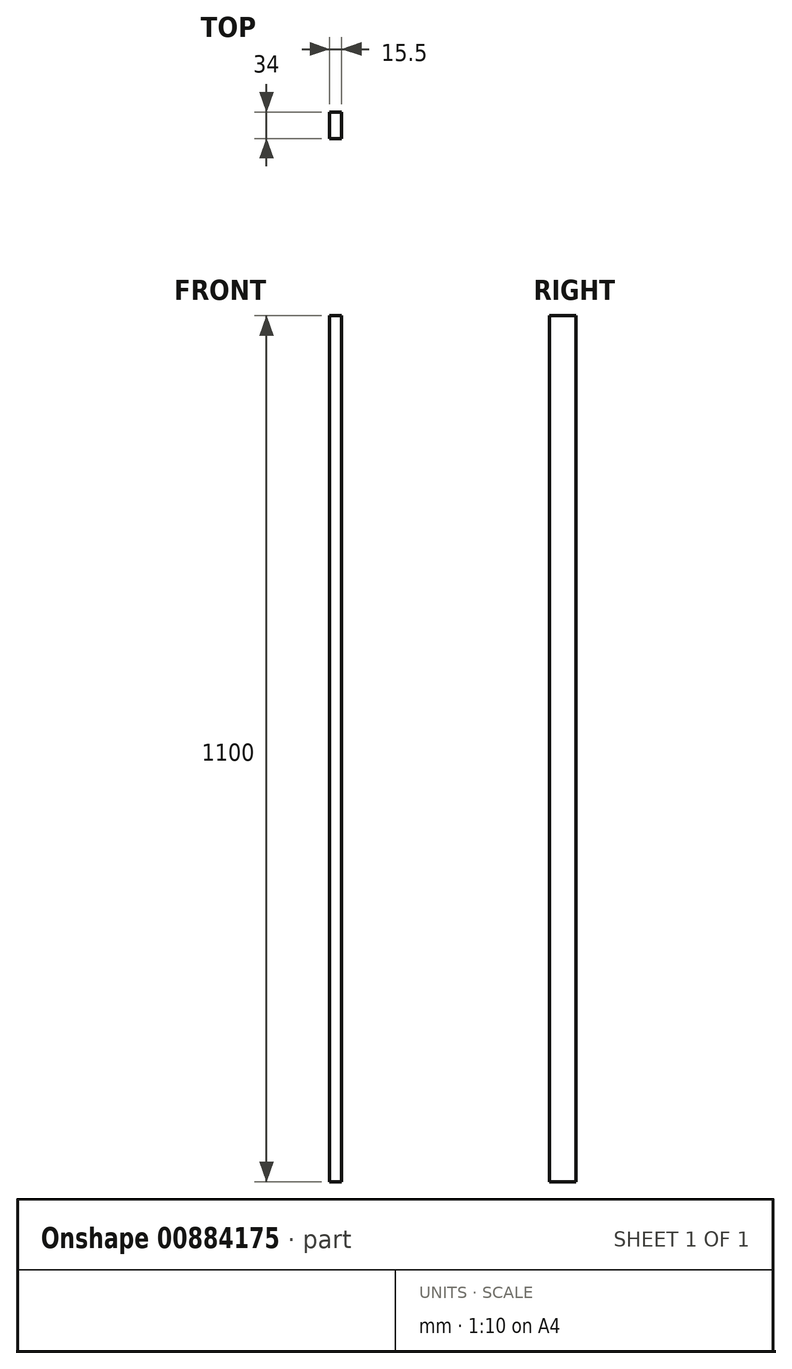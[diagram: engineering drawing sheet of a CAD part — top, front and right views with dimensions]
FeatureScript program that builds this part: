
annotation { "Feature Type Name" : "Feature", "Feature Type Description" : "" }
export const myFeature = defineFeature(function(context is Context, id is Id, definition is map)
    precondition{}
    {
        {
            var Q0;
            Q0=qCreatedBy(makeId("Top.planeOp"),FACE);
            var sketch = newSketch(context, id + "F0", { "sketchPlane" : qUnion([Q0])});
            skLineSegment(sketch, "E0.bottom", {"start": v(0, 0) * mm, "end": v(15.5, 0) * mm});
            skLineSegment(sketch, "E0.top", {"start": v(0, -34) * mm, "end": v(15.5, -34) * mm});
            skLineSegment(sketch, "E0.left", {"start": v(0, 0) * mm, "end": v(0, -34) * mm});
            skLineSegment(sketch, "E0.right", {"start": v(15.5, 0) * mm, "end": v(15.5, -34) * mm});
            skSolve(sketch);
        }
        {
            var Q0;
            Q0=qSketchRegion(id+"F0",true);
            extrude(context, id + "F1", {"entities" : qUnion([Q0]), "depth" : 1100 * mm, "offsetDistance" : 25 * mm});
        }
    });
